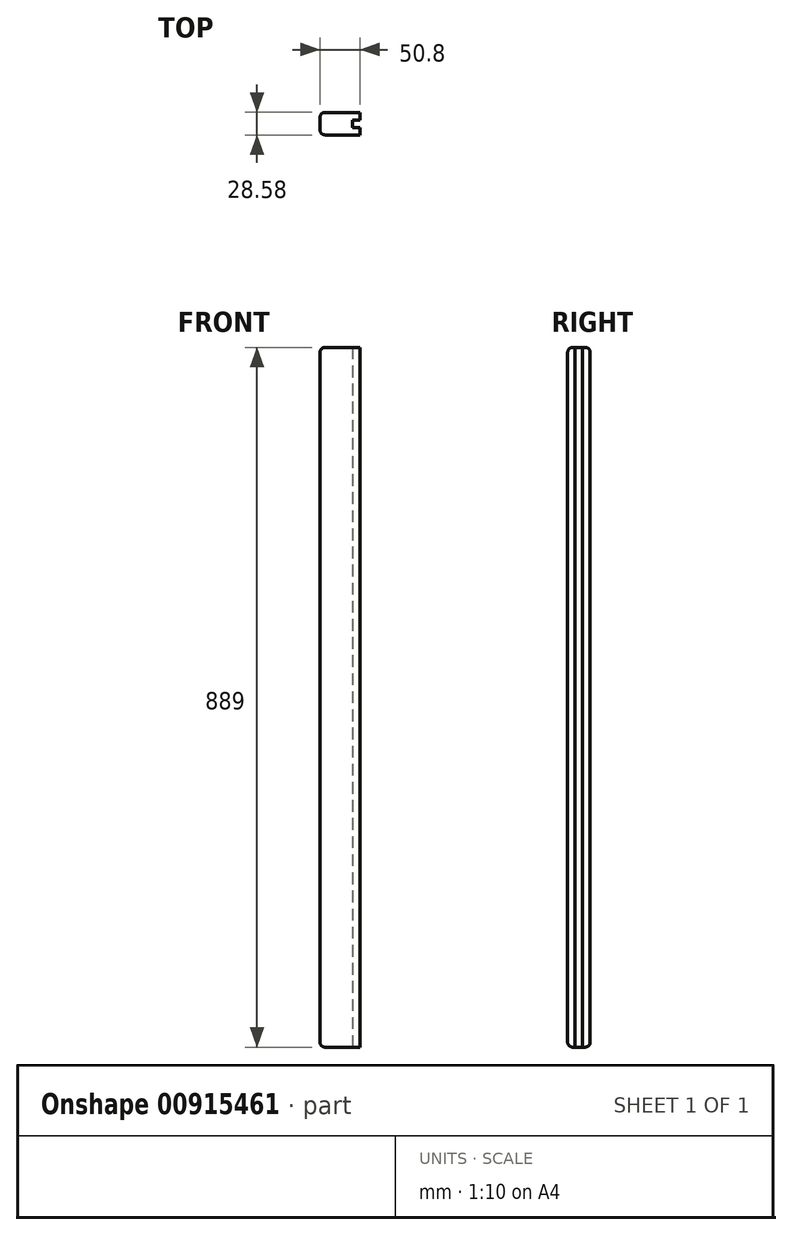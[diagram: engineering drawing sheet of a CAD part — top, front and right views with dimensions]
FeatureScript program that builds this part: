
annotation { "Feature Type Name" : "Feature", "Feature Type Description" : "" }
export const myFeature = defineFeature(function(context is Context, id is Id, definition is map)
    precondition{}
    {
        {
            var Q0;
            Q0=qCreatedBy(makeId("Top.planeOp"),FACE);
            var sketch = newSketch(context, id + "F0", { "sketchPlane" : qUnion([Q0])});
            skLineSegment(sketch, "E0.bottom", {"start": v(0, 0) * mm, "end": v(-50.8, 0) * mm});
            skLineSegment(sketch, "E0.top", {"start": v(0, 28.58) * mm, "end": v(-50.8, 28.58) * mm});
            skLineSegment(sketch, "E0.left", {"start": v(0, 0) * mm, "end": v(0, 9.53) * mm});
            skLineSegment(sketch, "E0.right", {"start": v(-50.8, 0) * mm, "end": v(-50.8, 28.58) * mm});
            skLineSegment(sketch, "E1", {"start": v(0, 19.05) * mm, "end": v(-9.53, 19.05) * mm});
            skLineSegment(sketch, "E2", {"start": v(-9.52, 19.05) * mm, "end": v(-9.52, 9.53) * mm});
            skLineSegment(sketch, "E3", {"start": v(-9.53, 9.53) * mm, "end": v(0, 9.53) * mm});
            skLineSegment(sketch, "E4.trimOffspring", {"start": v(0, 19.05) * mm, "end": v(0, 28.58) * mm});
            skSolve(sketch);
        }
        {
            var Q0;
            Q0=makeQuery(id+"F0.imprint","IMPRINT",FACE,{"disambiguationData":[TD([[makeQuery(id+"F0.imprint","IMPRINT",EDGE,{"derivedFrom":sQuery(id+"F0.wireOp",EDGE,"E0.bottom")}),-1.0]])]});
            extrude(context, id + "F1", {"entities" : qUnion([Q0]), "depth" : 889 * mm, "offsetDistance" : 25.4 * mm});
        }
        {
            var Q0;
            Q0=makeQuery(id+"F1.opExtrude","SWEPT_EDGE",EDGE,{"disambiguationData":[OSD([sQuery(id+"F0.wireOp",EDGE,"E0.bottom"),sQuery(id+"F0.wireOp",EDGE,"E0.right")])]});
            var Q1;
            Q1=makeQuery(id+"F1.opExtrude","SWEPT_EDGE",EDGE,{"disambiguationData":[OSD([sQuery(id+"F0.wireOp",EDGE,"E0.top"),sQuery(id+"F0.wireOp",EDGE,"E0.right")])]});
            var Q2;
            Q2=makeQuery(id+"F1.opExtrude","CAP_EDGE",EDGE,{"disambiguationData":[OSD([sQuery(id+"F0.wireOp",EDGE,"E0.top")])],"isStart":false});
            var Q3;
            Q3=makeQuery(id+"F1.opExtrude","CAP_EDGE",EDGE,{"disambiguationData":[OSD([sQuery(id+"F0.wireOp",EDGE,"E0.bottom")])],"isStart":true});
            var Q4;
            Q4=makeQuery(id+"F1.opExtrude","CAP_EDGE",EDGE,{"disambiguationData":[OSD([sQuery(id+"F0.wireOp",EDGE,"E0.top")])],"isStart":true});
            var Q5;
            Q5=makeQuery(id+"F1.opExtrude","CAP_EDGE",EDGE,{"disambiguationData":[OSD([sQuery(id+"F0.wireOp",EDGE,"E0.right")])],"isStart":true});
            var Q6;
            Q6=makeQuery(id+"F1.opExtrude","CAP_EDGE",EDGE,{"disambiguationData":[OSD([sQuery(id+"F0.wireOp",EDGE,"E0.bottom")])],"isStart":false});
            var Q7;
            Q7=makeQuery(id+"F1.opExtrude","CAP_EDGE",EDGE,{"disambiguationData":[OSD([sQuery(id+"F0.wireOp",EDGE,"E0.right")])],"isStart":false});
            fillet(context, id + "F2", {"entities" : qUnion([Q0, Q1, Q2, Q3, Q4, Q5, Q6, Q7]), "radius" : 6.35 * mm, "tangentPropagation" : true, "allowEdgeOverflow" : false});
        }
    });
